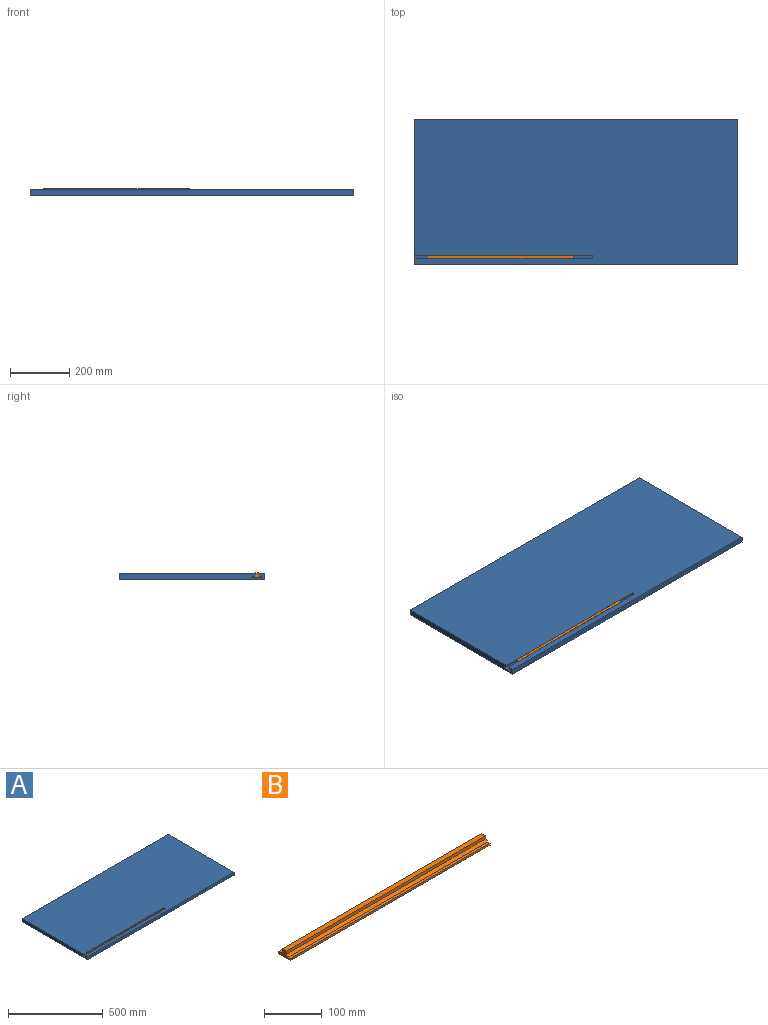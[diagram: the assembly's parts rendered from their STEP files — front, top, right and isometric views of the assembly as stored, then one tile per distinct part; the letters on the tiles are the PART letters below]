
ASSEMBLY  parts=2 mates=1
PART A: 16 faces, bbox 1090x490x20 mm
  f0: plane 1090x20mm, normal (0,1,0), area 21800mm2, adj f1,f3,f4,f14
  f1: plane 490x20mm, normal (-1,0,0), area 9495mm2, adj f0,f2,f3,f4,f5,f6,f7,f8
  f2: plane 1090x20mm, normal (0,-1,0), area 21800mm2, adj f1,f3,f4,f14
  f3: plane 1090x490mm, normal (0,0,1), area 526900mm2, adj f0,f1,f2,f5,f13,f14,f15
  f4: plane 1090x490mm, normal (0,0,-1), area 534100mm2, adj f0,f1,f2,f14
  f5: plane 600x5mm, normal (0,1,0), area 3000mm2, adj f1,f3,f6,f15
  f6: plane 600x5mm, normal (0,0.71,-0.71), area 4242.6mm2, adj f1,f5,f7,f15
  f7: plane 600x5mm, normal (0,0,-1), area 3000mm2, adj f1,f6,f8,f15
  f8: plane 600x5mm, normal (0,1,0), area 3000mm2, adj f1,f7,f9,f15
  f9: plane 600x32mm, normal (0,0,1), area 19200mm2, adj f1,f8,f10,f15
  f10: plane 600x5mm, normal (0,-1,0), area 3000mm2, adj f1,f9,f11,f15
  f11: plane 600x5mm, normal (0,0,-1), area 3000mm2, adj f1,f10,f12,f15
  f12: plane 600x5mm, normal (0,-0.71,-0.71), area 4242.6mm2, adj f1,f11,f13,f15
  f13: plane 600x5mm, normal (0,-1,0), area 3000mm2, adj f1,f3,f12,f15
  f14: plane 490x20mm, normal (1,0,0), area 9800mm2, adj f0,f2,f3,f4
  f15: plane 32x15mm, normal (-1,0,0), area 305mm2, adj f3,f5,f6,f7,f8,f9,f10,f11
PART B: 12 faces, bbox 490x30x15 mm
  f0: plane 490x30mm, normal (0,0,-1), area 14700mm2, adj f1,f9,f10,f11
  f1: plane 490x4mm, normal (0,1,0), area 1960mm2, adj f0,f2,f10,f11
  f2: plane 490x5.5mm, normal (0,0,1), area 2695mm2, adj f1,f3,f10,f11
  f3: plane 490x4.5mm, normal (0,0.71,0.71), area 3118.3mm2, adj f2,f4,f10,f11
  f4: plane 490x6.5mm, normal (0,1,0), area 3185mm2, adj f3,f5,f10,f11
  f5: plane 490x10mm, normal (0,0,1), area 4900mm2, adj f4,f6,f10,f11
  f6: plane 490x6.5mm, normal (0,-1,0), area 3185mm2, adj f5,f7,f10,f11
  f7: plane 490x4.5mm, normal (0,-0.71,0.71), area 3118.3mm2, adj f6,f8,f10,f11
  f8: plane 490x5.5mm, normal (0,0,1), area 2695mm2, adj f7,f9,f10,f11
  f9: plane 490x4mm, normal (0,-1,0), area 1960mm2, adj f0,f8,f10,f11
  f10: plane 30x15mm, normal (1,0,0), area 250.2mm2, adj f0,f1,f2,f3,f4,f5,f6,f7
  f11: plane 30x15mm, normal (-1,0,0), area 250.2mm2, adj f0,f1,f2,f3,f4,f5,f6,f7
PLACE A t=(-22.5,98.62,-57.31)mm fixed
PLACE B t=(-576.86,154.79,-87.87)mm
MATE slider B.f11 <-> A.f1  axis (-1,0,0) through (-276.86,-105.38,-51.81)mm
